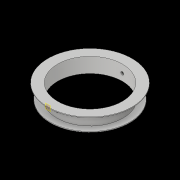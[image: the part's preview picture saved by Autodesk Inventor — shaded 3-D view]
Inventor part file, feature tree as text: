
AUTODESK INVENTOR PART (.ipt)
format: ipt  version: 2017 (Build 210142000, 142)  size: 139,776 bytes
history: native  units: in
note: dims shown in document units (in); Inventor stores cm internally (conversion verified against a paired STEP export)
features: sketch x2, revolve x1, plane x1, extrude x1
ambient origin geometry x8: Origin, YZ Plane, XZ Plane, XY Plane, X Axis, Y Axis, Z Axis, Center Point
bodies: Solid1 (feature_tree)
feature tree (5):
  revolve  "Revolution1"  [1 undecoded]
  plane  "Work Plane1"
  extrude  "Extrusion1"  Depth=0.125in
  sketch  "Sketch1"  dims[d0=2.0in d1=5.4375in]
  sketch  "Sketch2"  dims[d2=1.25in d3=0.125in d4=0.125in d5=2.25in d6=1.5in d7=0.125in d8=90.0deg d9=0.5in d10=1.0285in d11=1.0in d12=0.0in]
note: 1 required parameter value undecoded (feature->parameter linkage not recoverable at this tier; creation-order binding heuristic only, values carry confidence <= 0.55)
